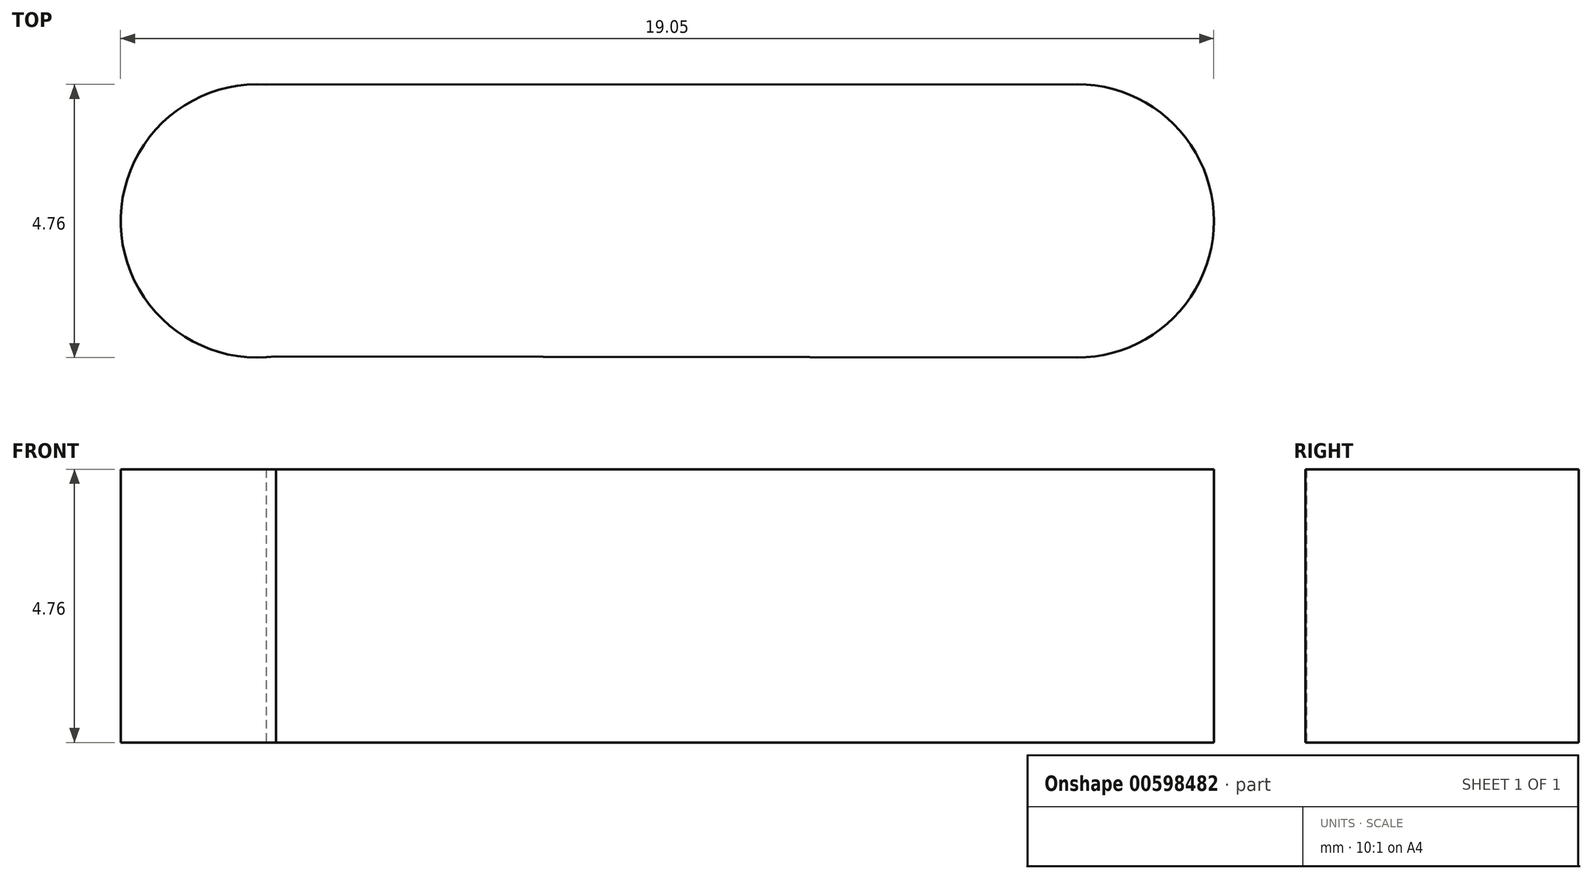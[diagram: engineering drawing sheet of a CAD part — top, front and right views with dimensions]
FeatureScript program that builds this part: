
annotation { "Feature Type Name" : "Feature", "Feature Type Description" : "" }
export const myFeature = defineFeature(function(context is Context, id is Id, definition is map)
    precondition{}
    {
        {
            var Q0;
            Q0=qCreatedBy(makeId("Top.planeOp"),FACE);
            var sketch = newSketch(context, id + "F0", { "sketchPlane" : qUnion([Q0])});
            skArc(sketch, "E0", {"start": v(-7.13, 2.38) * mm, "mid": v(-9.66, -0.08) * mm, "end": v(-6.96, -2.36) * mm});
            skArc(sketch, "E1", {"start": v(7, -2.38) * mm, "mid": v(9.38, 0) * mm, "end": v(7, 2.38) * mm});
            skLineSegment(sketch, "E2", {"start": v(-7.13, 2.38) * mm, "end": v(7, 2.38) * mm});
            skLineSegment(sketch, "E3", {"start": v(7, -2.38) * mm, "end": v(-6.96, -2.36) * mm});
            skSolve(sketch);
        }
        {
            var Q0;
            Q0=makeQuery(id+"F0.imprint","IMPRINT",FACE,{"disambiguationData":[TD([[makeQuery(id+"F0.imprint","IMPRINT",EDGE,{"derivedFrom":sQuery(id+"F0.wireOp",EDGE,"E0")}),1.0]])]});
            extrude(context, id + "F1", {"entities" : qUnion([Q0]), "depth" : 4.76 * mm, "offsetDistance" : 25.4 * mm});
        }
    });
